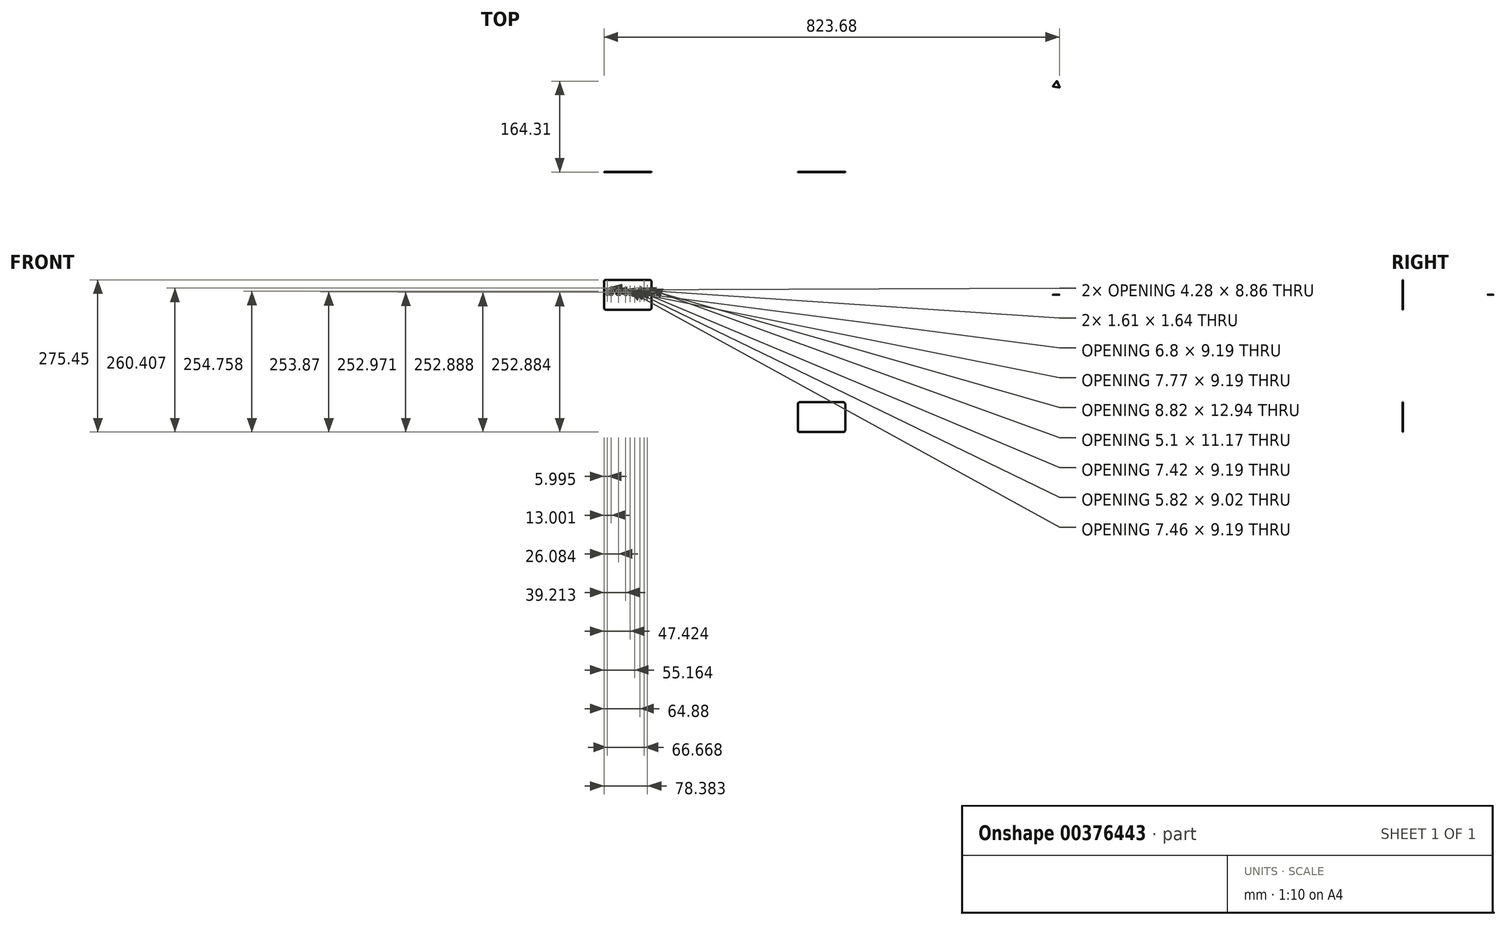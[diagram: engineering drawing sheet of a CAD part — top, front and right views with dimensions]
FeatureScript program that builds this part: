
annotation { "Feature Type Name" : "Feature", "Feature Type Description" : "" }
export const myFeature = defineFeature(function(context is Context, id is Id, definition is map)
    precondition{}
    {
        {
            var Q0;
            Q0=qCreatedBy(makeId("Front.planeOp"),FACE);
            var sketch = newSketch(context, id + "F0", { "sketchPlane" : qUnion([Q0])});
            skLineSegment(sketch, "E0.bottom", {"start": v(39.69, 26.99) * mm, "end": v(-39.69, 26.99) * mm});
            skLineSegment(sketch, "E0.top", {"start": v(39.69, -26.99) * mm, "end": v(-39.69, -26.99) * mm});
            skLineSegment(sketch, "E0.left", {"start": v(42.86, 23.81) * mm, "end": v(42.86, -23.81) * mm});
            skLineSegment(sketch, "E0.right", {"start": v(-42.86, 23.81) * mm, "end": v(-42.86, -23.81) * mm});
            skPoint(sketch, "E0.middle", {"position": v(0, 0) * mm});
            skPoint(sketch, "E1.visualSharp", {"position": v(42.86, 26.99) * mm});
            skArc(sketch, "E1.filletArc", {"start": v(42.86, 23.81) * mm, "mid": v(41.93, 26.06) * mm, "end": v(39.69, 26.99) * mm});
            skPoint(sketch, "E2.visualSharp", {"position": v(42.86, -26.99) * mm});
            skArc(sketch, "E2.filletArc", {"start": v(39.69, -26.99) * mm, "mid": v(41.93, -26.06) * mm, "end": v(42.86, -23.81) * mm});
            skPoint(sketch, "E3.visualSharp", {"position": v(-42.86, -26.99) * mm});
            skArc(sketch, "E3.filletArc", {"start": v(-42.86, -23.81) * mm, "mid": v(-41.93, -26.06) * mm, "end": v(-39.69, -26.99) * mm});
            skPoint(sketch, "E4.visualSharp", {"position": v(-42.86, 26.99) * mm});
            skArc(sketch, "E4.filletArc", {"start": v(-39.69, 26.99) * mm, "mid": v(-41.93, 26.06) * mm, "end": v(-42.86, 23.81) * mm});
            skText(sketch, "E5", { "text": "This is a credit card!", "fontName": "RobotoSlab-Regular.ttf"});
            const initialGuessF0  = {"E5": [-0.07929, 0, 1, 0, 0.01207]};
            skSetInitialGuess(sketch, initialGuessF0);
            skSolve(sketch);
        }
        {
            var Q0;
            Q0=makeQuery(id+"F0.imprint","IMPRINT",FACE,{"disambiguationData":[TD([[makeQuery(id+"F0.imprint","IMPRINT",EDGE,{"derivedFrom":sQuery(id+"F0.wireOp",EDGE,"E0.bottom")}),1.0]])]});
            extrude(context, id + "F1", {"entities" : qUnion([Q0]), "depth" : 0.6 * mm});
        }
        {
            var Q0;
            Q0=qCreatedBy(makeId("Front.planeOp"),FACE);
            var sketch = newSketch(context, id + "F2", { "sketchPlane" : qUnion([Q0])});
            skLineSegment(sketch, "E6.bottom", {"start": v(390.1, -194.49) * mm, "end": v(310.72, -194.49) * mm});
            skLineSegment(sketch, "E6.top", {"start": v(390.1, -248.46) * mm, "end": v(310.72, -248.46) * mm});
            skLineSegment(sketch, "E6.left", {"start": v(393.27, -197.66) * mm, "end": v(393.27, -245.29) * mm});
            skLineSegment(sketch, "E6.right", {"start": v(307.54, -197.66) * mm, "end": v(307.54, -245.29) * mm});
            skPoint(sketch, "E6.middle", {"position": v(350.4, -221.47) * mm});
            skPoint(sketch, "E7.visualSharp", {"position": v(393.27, -248.46) * mm});
            skArc(sketch, "E7.filletArc", {"start": v(390.1, -248.46) * mm, "mid": v(392.34, -247.53) * mm, "end": v(393.27, -245.29) * mm});
            skPoint(sketch, "E8.visualSharp", {"position": v(393.27, -194.49) * mm});
            skArc(sketch, "E8.filletArc", {"start": v(393.27, -197.66) * mm, "mid": v(392.34, -195.42) * mm, "end": v(390.1, -194.49) * mm});
            skPoint(sketch, "E9.visualSharp", {"position": v(307.54, -194.49) * mm});
            skArc(sketch, "E9.filletArc", {"start": v(310.72, -194.49) * mm, "mid": v(308.47, -195.42) * mm, "end": v(307.54, -197.66) * mm});
            skPoint(sketch, "E10.visualSharp", {"position": v(307.54, -248.46) * mm});
            skArc(sketch, "E10.filletArc", {"start": v(307.54, -245.29) * mm, "mid": v(308.47, -247.53) * mm, "end": v(310.72, -248.46) * mm});
            skSolve(sketch);
        }
        {
            var Q0;
            Q0 = qSketchRegion(id + "F2", true);
            extrude(context, id + "F3", {"entities" : qUnion([Q0]), "depth" : 0.6 * mm});
        }
        {
            var Q0;
            Q0=qCreatedBy(makeId("Top.planeOp"),FACE);
            var sketch = newSketch(context, id + "F4", { "sketchPlane" : qUnion([Q0])});
            skCircle(sketch, "E11.cCircle", {"center": v(775.29, 156.84) * mm, "radius": 3.67 * mm, "construction": true});
            skLineSegment(sketch, "E11.0", {"start": v(776.6, 163.46) * mm, "end": v(780.8, 152.93) * mm});
            skLineSegment(sketch, "E11.1", {"start": v(780.36, 152.4) * mm, "end": v(769.16, 154.03) * mm});
            skLineSegment(sketch, "E11.2", {"start": v(768.9, 154.66) * mm, "end": v(775.92, 163.55) * mm});
            skPoint(sketch, "E11.0.midPoint", {"position": v(778.7, 158.2) * mm});
            skPoint(sketch, "E12.visualSharp", {"position": v(776.34, 164.1) * mm});
            skArc(sketch, "E12.filletArc", {"start": v(776.6, 163.46) * mm, "mid": v(776.29, 163.7) * mm, "end": v(775.92, 163.55) * mm});
            skPoint(sketch, "E13.visualSharp", {"position": v(768.48, 154.13) * mm});
            skArc(sketch, "E13.filletArc", {"start": v(768.9, 154.66) * mm, "mid": v(768.85, 154.27) * mm, "end": v(769.16, 154.03) * mm});
            skPoint(sketch, "E14.visualSharp", {"position": v(781.04, 152.3) * mm});
            skArc(sketch, "E14.filletArc", {"start": v(780.36, 152.4) * mm, "mid": v(780.73, 152.54) * mm, "end": v(780.8, 152.93) * mm});
            skSolve(sketch);
        }
        {
            var Q0;
            Q0 = qSketchRegion(id + "F4", true);
            extrude(context, id + "F5", {"entities" : qUnion([Q0]), "depth" : 3 / 406.4 * mm, "hasDraft" : true, "draftAngle" : 4 * degree});
        }
    });
